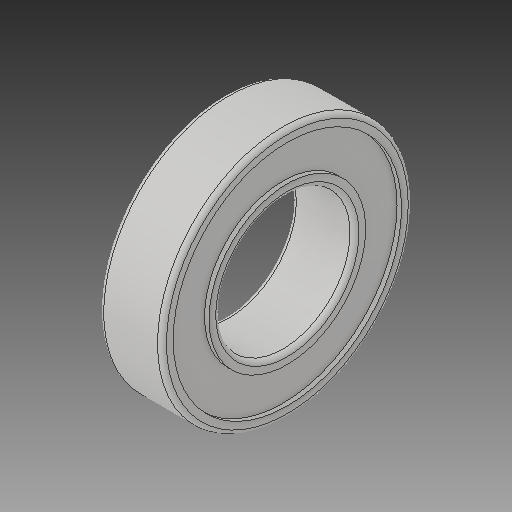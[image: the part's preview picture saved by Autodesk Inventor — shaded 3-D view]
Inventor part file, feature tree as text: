
AUTODESK INVENTOR PART (.ipt)
format: ipt  version: 2017 (Build 210142000, 142)  size: 177,152 bytes
history: native  units: in
note: dims shown in document units (in); Inventor stores cm internally (conversion verified against a paired STEP export)
features: fillet x1
ambient origin geometry x8: Origin, YZ Plane, XZ Plane, XY Plane, X Axis, Y Axis, Z Axis, Center Point
bodies: Solid1 (feature_tree)
feature tree (1):
  fillet  "Fillet1"  [1 undecoded]
note: 1 required parameter value undecoded (feature->parameter linkage not recoverable at this tier; creation-order binding heuristic only, values carry confidence <= 0.55)
